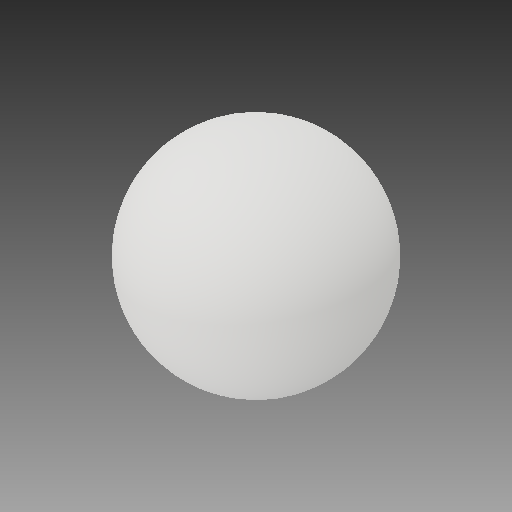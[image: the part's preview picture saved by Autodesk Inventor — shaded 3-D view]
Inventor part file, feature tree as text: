
AUTODESK INVENTOR PART (.ipt)
format: ipt  version: 2017 (Build 210142000, 142)  size: 117,248 bytes
history: native  units: in
note: dims shown in document units (in); Inventor stores cm internally (conversion verified against a paired STEP export)
features: revolve x1
ambient origin geometry x8: Origin, YZ Plane, XZ Plane, XY Plane, X Axis, Y Axis, Z Axis, Center Point
bodies: Solid1 (feature_tree)
feature tree (1):
  revolve  "Revolve1"  [1 undecoded]
note: 1 required parameter value undecoded (feature->parameter linkage not recoverable at this tier; creation-order binding heuristic only, values carry confidence <= 0.55)
